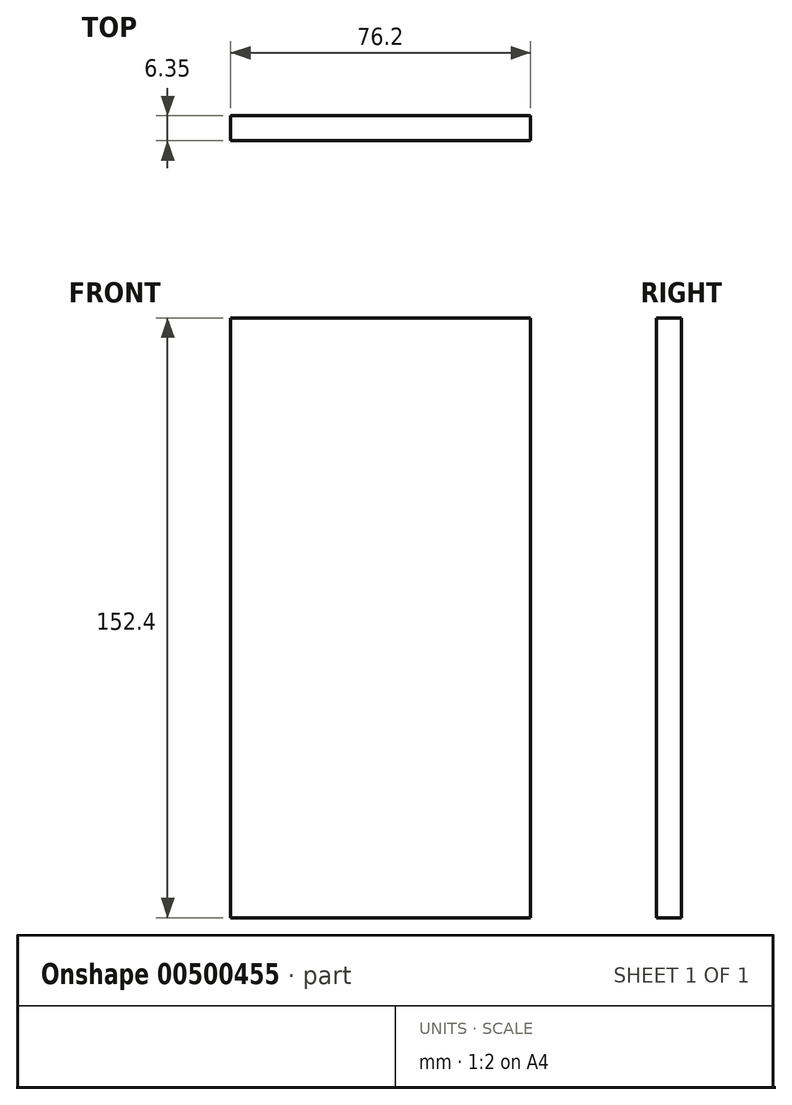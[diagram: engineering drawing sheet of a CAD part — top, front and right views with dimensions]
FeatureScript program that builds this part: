
annotation { "Feature Type Name" : "Feature", "Feature Type Description" : "" }
export const myFeature = defineFeature(function(context is Context, id is Id, definition is map)
    precondition{}
    {
        {
            var Q0;
            Q0=qCreatedBy(makeId("Front.planeOp"),FACE);
            var sketch = newSketch(context, id + "F0", { "sketchPlane" : qUnion([Q0])});
            skLineSegment(sketch, "E0.bottom", {"start": v(-33.32, 74.1) * mm, "end": v(42.88, 74.1) * mm});
            skLineSegment(sketch, "E0.top", {"start": v(-33.32, -78.3) * mm, "end": v(42.88, -78.3) * mm});
            skLineSegment(sketch, "E0.left", {"start": v(-33.32, 74.1) * mm, "end": v(-33.32, -78.3) * mm});
            skLineSegment(sketch, "E0.right", {"start": v(42.88, 74.1) * mm, "end": v(42.88, -78.3) * mm});
            skSolve(sketch);
        }
        {
            var Q0;
            Q0=makeQuery(id+"F0.imprint","IMPRINT",FACE,{"disambiguationData":[TD([[makeQuery(id+"F0.imprint","IMPRINT",EDGE,{"derivedFrom":sQuery(id+"F0.wireOp",EDGE,"E0.bottom")}),-1.0]])]});
            extrude(context, id + "F1", {"entities" : qUnion([Q0]), "depth" : 6.35 * mm});
        }
    });
